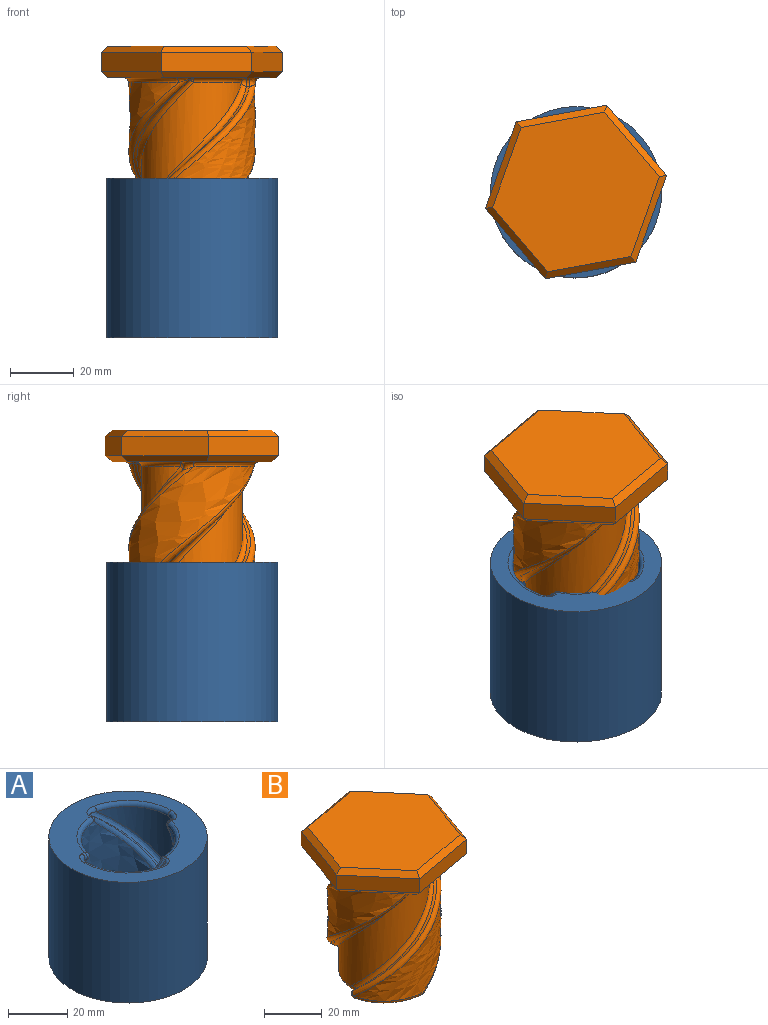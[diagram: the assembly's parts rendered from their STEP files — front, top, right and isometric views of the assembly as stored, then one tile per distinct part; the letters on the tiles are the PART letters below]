
ASSEMBLY  parts=2 mates=1
PART A: 51 faces, bbox 53.6x53.6x54.5 mm
  f0: cylinder r=19.82mm len=47mm, axis (0,0,-1), area 1230.7mm2, adj f33,f34,f44,f45
  f1: cylinder r=19.82mm len=47mm, axis (0,0,-1), area 1230.7mm2, adj f17,f18,f26,f27
  f2: cylinder r=26.82mm len=53.64mm, axis (0,0,-1), area 8426mm2, adj f3,f4
  f3: plane 53.64x53.64mm, normal (0,0,1), area 1049.9mm2, adj f2,f16,f21,f25,f26,f31,f35,f36
  f4: plane 53.64x53.64mm, normal (0,0,-1), area 1049.9mm2, adj f2,f11,f13,f14,f18,f22,f23,f28
  f5: bspline ~50x39.64mm, area 70.7mm2, adj f11,f15,f16,f17
  f6: bspline ~50x34.48mm, area 977.8mm2, adj f14,f15,f24,f25
  f7: bspline ~50x39.64mm, area 70.7mm2, adj f23,f24,f34,f35
  f8: bspline ~50x39.64mm, area 70.7mm2, adj f27,f28,f36,f37
  f9: bspline ~50x39.64mm, area 70.7mm2, adj f39,f44,f47,f50
  f10: bspline ~50x34.48mm, area 977.8mm2, adj f37,f38,f46,f47
  f11: bspline ~1.52x1.02mm, area 1.1mm2, adj f4,f5,f12,f13
  f12: sphere r=1.5mm, area 2.1mm2, adj f11,f14,f15
  f13: bspline ~5.83x3.03mm, area 8.8mm2, adj f4,f11,f17,f18
  f14: bspline ~17.88x15.12mm, area 50.7mm2, adj f4,f6,f12,f19
  f15: bspline ~50.12x34.53mm, area 154.7mm2, adj f5,f6,f12,f20
  f16: bspline ~4.03x2.65mm, area 3.6mm2, adj f3,f5,f20,f21
  f17: bspline ~52.74x39.71mm, area 177.7mm2, adj f1,f5,f13,f21
  f18: torus R=21.32mm, axis (0,0,1), area 63.4mm2, adj f1,f4,f13,f22
  f19: sphere r=1.5mm, area 4.9mm2, adj f14,f23,f24
  f20: sphere r=1.5mm, area 5.7mm2, adj f15,f16,f25
  f21: bspline ~6.05x3.74mm, area 13.9mm2, adj f3,f16,f17,f26
  f22: bspline ~6.05x3.74mm, area 13.9mm2, adj f4,f18,f27,f28
  f23: bspline ~4.03x2.65mm, area 3.6mm2, adj f4,f7,f19,f29
  f24: bspline ~49.09x34.41mm, area 154.7mm2, adj f6,f7,f19,f30
  f25: bspline ~17.88x15.12mm, area 50.7mm2, adj f3,f6,f20,f30
  f26: torus R=21.32mm, axis (0,0,1), area 63.4mm2, adj f1,f3,f21,f31
  f27: bspline ~52.78x39.71mm, area 177.7mm2, adj f1,f8,f22,f31
  f28: bspline ~4.03x2.65mm, area 3.6mm2, adj f4,f8,f22,f32
  f29: bspline ~6.05x3.74mm, area 13.9mm2, adj f4,f23,f33,f34
  f30: sphere r=1.5mm, area 1.8mm2, adj f24,f25,f35
  f31: bspline ~5.83x3.03mm, area 8.8mm2, adj f3,f26,f27,f36
  f32: sphere r=1.5mm, area 3.6mm2, adj f28,f37,f38
  f33: torus R=21.32mm, axis (0,0,1), area 63.4mm2, adj f0,f4,f29,f40
  f34: bspline ~52.78x39.71mm, area 177.7mm2, adj f0,f7,f29,f41
  f35: bspline ~1.52x1.02mm, area 1.1mm2, adj f3,f7,f30,f41
  f36: bspline ~1.52x1.02mm, area 1.1mm2, adj f3,f8,f31,f42
  f37: bspline ~49.09x34.41mm, area 154.7mm2, adj f8,f10,f32,f42
  f38: bspline ~17.88x15.12mm, area 50.7mm2, adj f4,f10,f32,f43
  f39: bspline ~1.52x1.02mm, area 1.1mm2, adj f4,f9,f40,f43
  f40: bspline ~5.83x3.03mm, area 8.8mm2, adj f4,f33,f39,f44
  f41: bspline ~5.83x3.03mm, area 8.8mm2, adj f3,f34,f35,f45
  f42: sphere r=1.5mm, area 2.1mm2, adj f36,f37,f46
  f43: sphere r=1.5mm, area 2.4mm2, adj f38,f39,f47
  f44: bspline ~52.74x39.71mm, area 177.7mm2, adj f0,f9,f40,f48
  f45: torus R=21.32mm, axis (0,0,1), area 63.4mm2, adj f0,f3,f41,f48
  f46: bspline ~17.88x15.12mm, area 50.7mm2, adj f3,f10,f42,f49
  f47: bspline ~50.12x34.53mm, area 154.7mm2, adj f9,f10,f43,f49
  f48: bspline ~6.05x3.74mm, area 13.9mm2, adj f3,f44,f45,f50
  f49: sphere r=1.5mm, area 4.7mm2, adj f46,f47,f50
  f50: bspline ~4.03x2.65mm, area 3.6mm2, adj f3,f9,f48,f49
PART B: 69 faces, bbox 56.8x54.4x61.6 mm
  f0: plane 36.63x35.77mm, normal (0,0,-1), area 825.3mm2, adj f24,f25,f29,f34,f35,f39,f45,f49
  f1: cylinder r=15.82mm len=47mm, axis (0,0,-1), area 977.7mm2, adj f43,f44,f52,f53
  f2: cylinder r=15.82mm len=47mm, axis (0,0,-1), area 977.7mm2, adj f20,f21,f29,f30
  f3: bspline ~50x39.64mm, area 67.4mm2, adj f32,f33,f44,f45
  f4: bspline ~50x43.2mm, area 1230.9mm2, adj f22,f23,f33,f34
  f5: bspline ~50x39.64mm, area 74.9mm2, adj f17,f20,f23,f24
  f6: bspline ~50x43.2mm, area 1230.9mm2, adj f40,f41,f50,f51
  f7: bspline ~50x39.64mm, area 74.9mm2, adj f42,f51,f52,f56
  f8: bspline ~50x39.64mm, area 67.4mm2, adj f30,f31,f39,f40
  f9: plane 52.25x50.03mm, normal (0,0,-1), area 622.4mm2, adj f17,f19,f21,f22,f27,f31,f32,f36
  f10: plane 27.19x9.7mm, normal (0.94,-0.34,0), area 173.2mm2, adj f11,f15,f57,f67
  f11: plane 22x18.7mm, normal (0.76,0.65,0), area 173.2mm2, adj f10,f12,f59,f68
  f12: plane 28.4x6mm, normal (-0.18,0.98,0), area 173.2mm2, adj f11,f13,f61,f66
  f13: plane 27.19x9.7mm, normal (-0.94,0.34,0), area 173.2mm2, adj f12,f14,f62,f64
  f14: plane 22x18.7mm, normal (-0.76,-0.65,0), area 173.2mm2, adj f13,f15,f60,f63
  f15: plane 28.4x6mm, normal (0.18,-0.98,0), area 173.2mm2, adj f10,f14,f58,f65
  f16: plane 52.25x50.03mm, normal (0,0,1), area 1832.5mm2, adj f63,f64,f65,f66,f67,f68
  f17: bspline ~1.53x1.02mm, area 1.1mm2, adj f5,f9,f18,f19
  f18: sphere r=1.5mm, area 2.1mm2, adj f17,f20,f21
  f19: bspline ~6.49x2.81mm, area 8.7mm2, adj f9,f17,f22,f23
  f20: bspline ~51.69x34.59mm, area 158.3mm2, adj f2,f5,f18,f25
  f21: torus R=17.32mm, axis (0,0,1), area 50.7mm2, adj f2,f9,f18,f26
  f22: bspline ~21.35x18.02mm, area 63.4mm2, adj f4,f9,f19,f27
  f23: bspline ~51.36x39.68mm, area 181.9mm2, adj f4,f5,f19,f28
  f24: bspline ~1.8x1.02mm, area 1.1mm2, adj f0,f5,f25,f28
  f25: bspline ~4.24x3.69mm, area 7.5mm2, adj f0,f20,f24,f29
  f26: sphere r=1.5mm, area 7mm2, adj f21,f30,f31
  f27: bspline ~5.31x3.73mm, area 13.9mm2, adj f9,f22,f32,f33
  f28: sphere r=1.5mm, area 2.2mm2, adj f23,f24,f34
  f29: torus R=14.32mm, axis (0,0,1), area 47.3mm2, adj f0,f2,f25,f35
  f30: bspline ~51.48x34.55mm, area 151mm2, adj f2,f8,f26,f35
  f31: bspline ~4.02x2.65mm, area 3.6mm2, adj f8,f9,f26,f36
  f32: bspline ~4.02x2.65mm, area 3.6mm2, adj f3,f9,f27,f37
  f33: bspline ~49.64x39.56mm, area 173.4mm2, adj f3,f4,f27,f38
  f34: bspline ~20.19x16.77mm, area 60mm2, adj f0,f4,f28,f38
  f35: bspline ~5.23x3.71mm, area 11.8mm2, adj f0,f29,f30,f39
  f36: bspline ~5.31x3.94mm, area 13.9mm2, adj f9,f31,f40,f41
  f37: sphere r=1.5mm, area 7mm2, adj f32,f43,f44
  f38: sphere r=1.5mm, area 3.2mm2, adj f33,f34,f45
  f39: bspline ~4.08x2.79mm, area 3.6mm2, adj f0,f8,f35,f46
  f40: bspline ~49.64x39.56mm, area 173.4mm2, adj f6,f8,f36,f46
  f41: bspline ~21.35x18.02mm, area 63.4mm2, adj f6,f9,f36,f47
  f42: bspline ~1.53x1.02mm, area 1.1mm2, adj f7,f9,f47,f48
  f43: torus R=17.32mm, axis (0,0,1), area 50.7mm2, adj f1,f9,f37,f48
  f44: bspline ~51.48x34.55mm, area 151mm2, adj f1,f3,f37,f49
  f45: bspline ~4.08x2.79mm, area 3.6mm2, adj f0,f3,f38,f49
  f46: sphere r=1.5mm, area 5.1mm2, adj f39,f40,f50
  f47: bspline ~6.49x2.81mm, area 8.7mm2, adj f9,f41,f42,f51
  f48: sphere r=1.5mm, area 2.1mm2, adj f42,f43,f52
  f49: bspline ~5.23x3.71mm, area 11.8mm2, adj f0,f44,f45,f53
  f50: bspline ~20.19x16.77mm, area 60mm2, adj f0,f6,f46,f54
  f51: bspline ~51.36x39.68mm, area 181.9mm2, adj f6,f7,f47,f54
  f52: bspline ~51.69x34.59mm, area 158.3mm2, adj f1,f7,f48,f55
  f53: torus R=14.32mm, axis (0,0,1), area 47.3mm2, adj f0,f1,f49,f55
  f54: sphere r=1.5mm, area 1.6mm2, adj f50,f51,f56
  f55: bspline ~4.24x3.69mm, area 7.5mm2, adj f0,f52,f53,f56
  f56: bspline ~1.8x1.02mm, area 1.1mm2, adj f0,f7,f54,f55
  f57: plane 27.19x11.2mm, normal (0.67,-0.24,-0.71), area 78.4mm2, adj f9,f10,f58,f59
  f58: plane 28.4x6.95mm, normal (0.13,-0.7,-0.71), area 78.4mm2, adj f9,f15,f57,f60
  f59: plane 22.41x19.47mm, normal (0.54,0.46,-0.71), area 78.4mm2, adj f9,f11,f57,f61
  f60: plane 22.41x19.47mm, normal (-0.54,-0.46,-0.71), area 78.4mm2, adj f9,f14,f58,f62
  f61: plane 28.4x6.95mm, normal (-0.13,0.7,-0.71), area 78.4mm2, adj f9,f12,f59,f62
  f62: plane 27.19x11.2mm, normal (-0.67,0.24,-0.71), area 78.4mm2, adj f9,f13,f60,f61
  f63: plane 22.41x19.47mm, normal (-0.54,-0.46,0.71), area 78.4mm2, adj f14,f16,f64,f65
  f64: plane 27.19x11.2mm, normal (-0.67,0.24,0.71), area 78.4mm2, adj f13,f16,f63,f66
  f65: plane 28.4x6.95mm, normal (0.13,-0.7,0.71), area 78.4mm2, adj f15,f16,f63,f67
  f66: plane 28.4x6.95mm, normal (-0.13,0.7,0.71), area 78.4mm2, adj f12,f16,f64,f68
  f67: plane 27.19x11.2mm, normal (0.67,-0.24,0.71), area 78.4mm2, adj f10,f16,f65,f68
  f68: plane 22.41x19.47mm, normal (0.54,0.46,0.71), area 78.4mm2, adj f11,f16,f66,f67
PLACE A rot(axis=(0,0,1),113.3deg) t=(60.34,56.95,0)mm
PLACE B t=(-79.88,-0.07,31.48)mm
MATE cylindrical B.f1 <-> A.f0  axis (0,0,-1) through (6.48,51.53,31.48)mm
